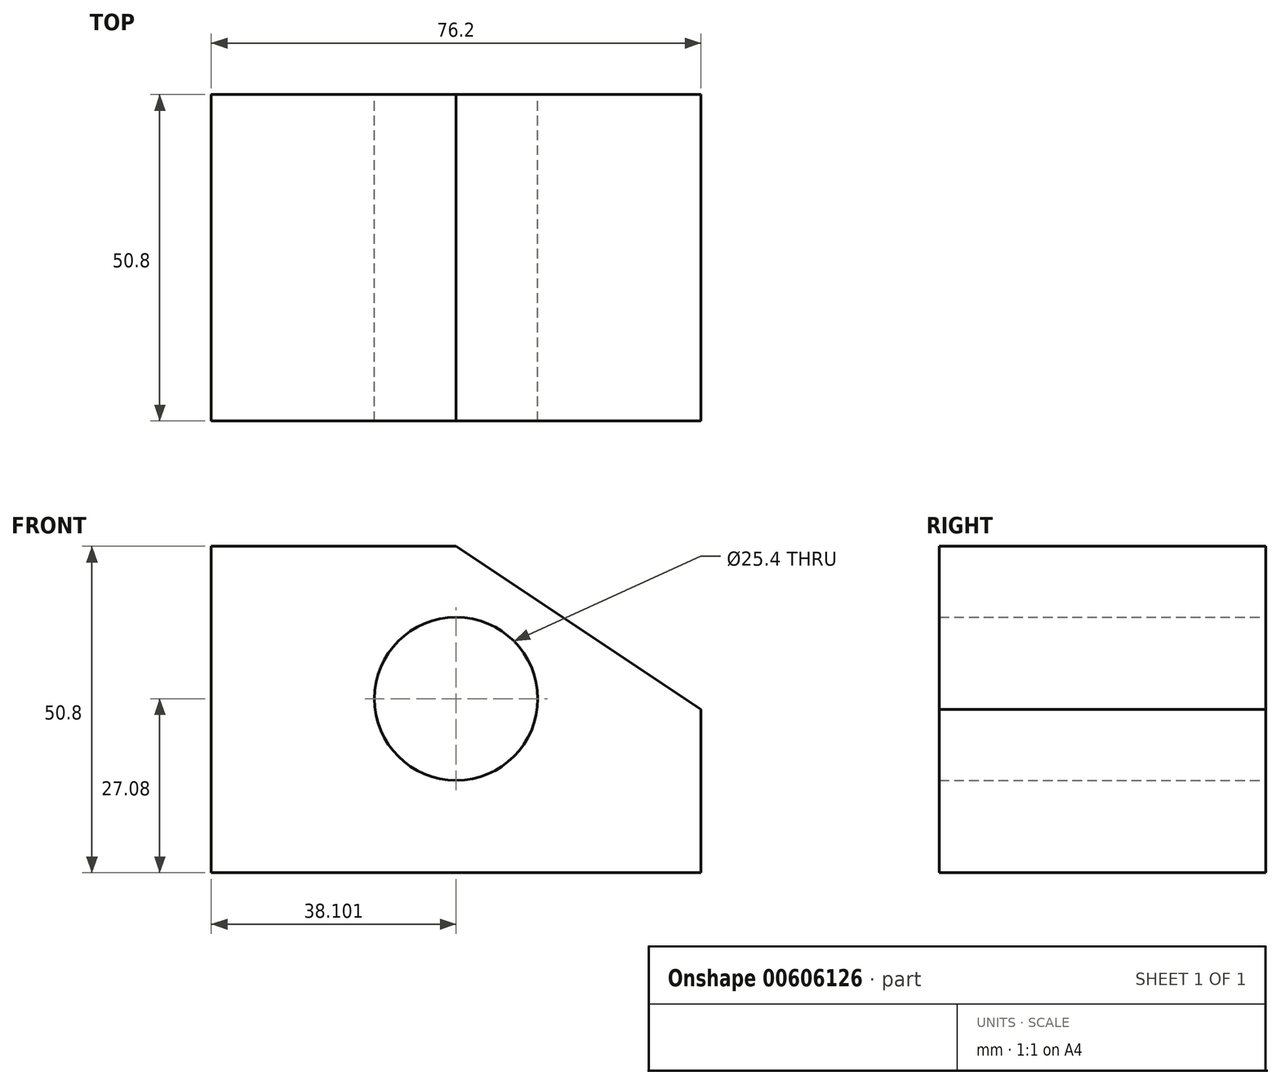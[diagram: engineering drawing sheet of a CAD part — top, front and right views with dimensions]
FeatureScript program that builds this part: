
annotation { "Feature Type Name" : "Feature", "Feature Type Description" : "" }
export const myFeature = defineFeature(function(context is Context, id is Id, definition is map)
    precondition{}
    {
        {
            var Q0;
            Q0=qCreatedBy(makeId("Front.planeOp"),FACE);
            var sketch = newSketch(context, id + "F0", { "sketchPlane" : qUnion([Q0])});
            skLineSegment(sketch, "E0", {"start": v(-49.25, 23.72) * mm, "end": v(-49.25, -27.08) * mm});
            skLineSegment(sketch, "E1", {"start": v(-49.25, -27.08) * mm, "end": v(26.95, -27.08) * mm});
            skLineSegment(sketch, "E2", {"start": v(26.95, -27.08) * mm, "end": v(26.95, -1.68) * mm});
            skLineSegment(sketch, "E3", {"start": v(-49.25, 23.72) * mm, "end": v(-11.15, 23.72) * mm});
            skLineSegment(sketch, "E4", {"start": v(-11.15, 23.72) * mm, "end": v(26.95, -1.68) * mm});
            skCircle(sketch, "E5", {"center": v(-11.15, 0) * mm, "radius": 12.7 * mm});
            skSolve(sketch);
        }
        {
            var Q0;
            Q0=makeQuery(id+"F0.imprint","IMPRINT",FACE,{"disambiguationData":[TD([[makeQuery(id+"F0.imprint","IMPRINT",EDGE,{"derivedFrom":sQuery(id+"F0.wireOp",EDGE,"E0")}),1.0]])]});
            extrude(context, id + "F1", {"entities" : qUnion([Q0]), "depth" : 50.8 * mm, "offsetDistance" : 25.4 * mm});
        }
    });
